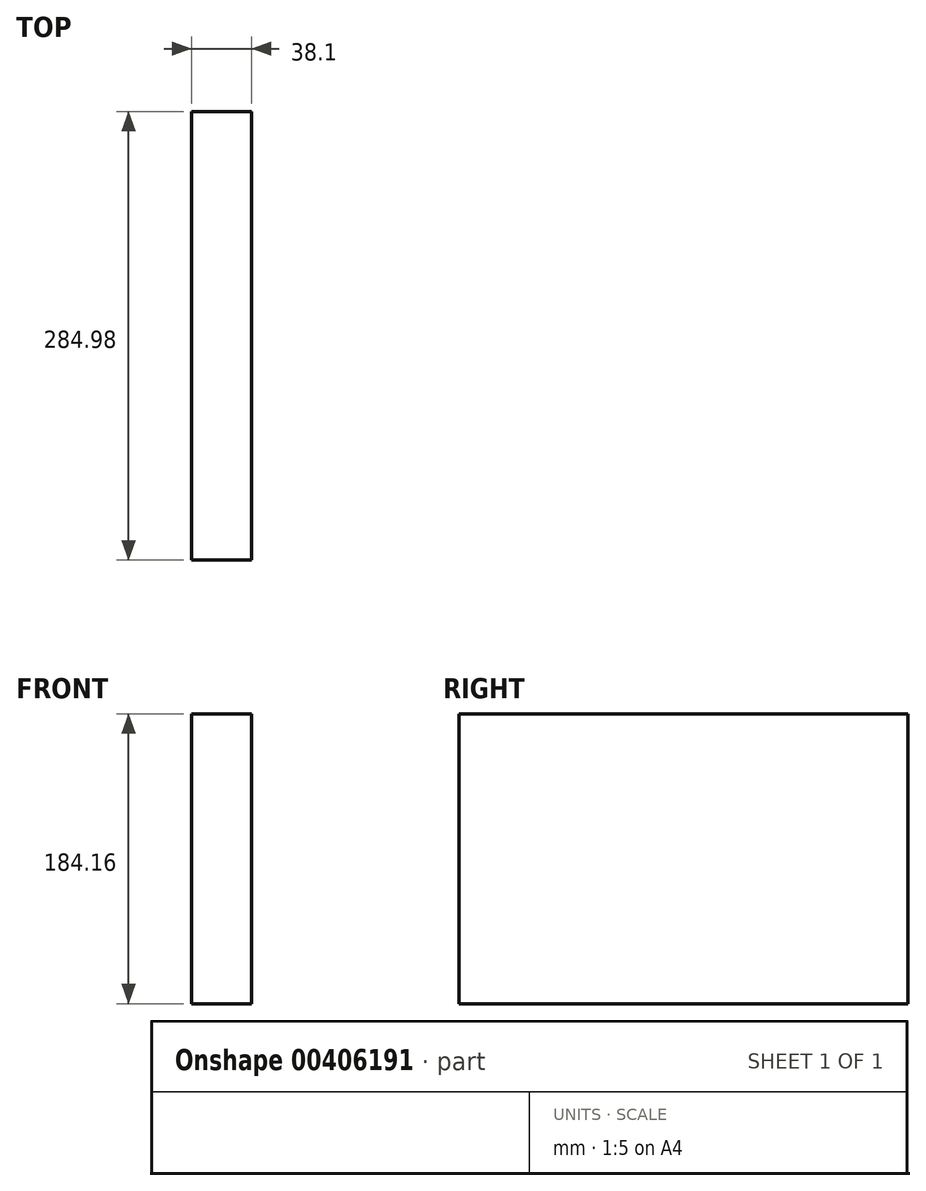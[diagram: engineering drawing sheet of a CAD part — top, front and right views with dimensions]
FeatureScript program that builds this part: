
annotation { "Feature Type Name" : "Feature", "Feature Type Description" : "" }
export const myFeature = defineFeature(function(context is Context, id is Id, definition is map)
    precondition{}
    {
        {
            var Q0;
            Q0=qCreatedBy(makeId("Front.planeOp"),FACE);
            var sketch = newSketch(context, id + "F0", { "sketchPlane" : qUnion([Q0])});
            skLineSegment(sketch, "E0.bottom", {"start": v(-19.05, -92.08) * mm, "end": v(19.05, -92.08) * mm});
            skLineSegment(sketch, "E0.top", {"start": v(-19.05, 92.08) * mm, "end": v(19.05, 92.08) * mm});
            skLineSegment(sketch, "E0.left", {"start": v(-19.05, -92.08) * mm, "end": v(-19.05, 92.07) * mm});
            skLineSegment(sketch, "E0.right", {"start": v(19.05, -92.08) * mm, "end": v(19.05, 92.08) * mm});
            skPoint(sketch, "E0.middle", {"position": v(0, 0) * mm});
            skSolve(sketch);
        }
        {
            var Q0;
            Q0=makeQuery(id+"F0.imprint","IMPRINT",FACE,{"disambiguationData":[TD([[makeQuery(id+"F0.imprint","IMPRINT",EDGE,{"derivedFrom":sQuery(id+"F0.wireOp",EDGE,"E0.bottom")}),1.0]])]});
            var sketch = newSketch(context, id + "F1", { "sketchPlane" : qUnion([Q0])});
            skSolve(sketch);
        }
        {
            var Q0;
            Q0=makeQuery(id+"F1.imprint","IMPRINT",FACE,{"disambiguationData":[TD([[makeQuery(id+"F1.imprint","IMPRINT",EDGE,{"derivedFrom":makeQuery(id+"F0.imprint","IMPRINT",EDGE,{"derivedFrom":sQuery(id+"F0.wireOp",EDGE,"E0.bottom")})}),1.0]])]});
            extrude(context, id + "F2", {"entities" : qUnion([Q0]), "oppositeDirection" : true, "depth" : 284.98 * mm});
        }
    });
